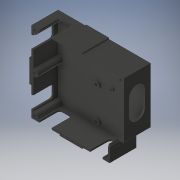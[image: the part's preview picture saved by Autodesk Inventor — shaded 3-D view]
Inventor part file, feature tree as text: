
AUTODESK INVENTOR PART (.ipt)
format: ipt  version: 2019.4 (Build 234330000, 330)  size: 476,160 bytes
history: native  units: mm
features: extrude x19, hole x4, sketch x3, fillet x1, projected_geometry x1
ambient origin geometry x8: Origin, YZ Plane, XZ Plane, XY Plane, X Axis, Y Axis, Z Axis, Center Point
bodies: Solid1 (feature_tree)
feature tree (28):
  sketch  "Sketch1"  dims[d0=147.0mm d1=128.0mm]
  extrude  "Extrusion1"  Depth=128.0mm
  extrude  "Extrusion2"  Depth=37.0mm
  extrude  "Extrusion3"  Depth=2.0mm
  extrude  "Extrusion4"  Depth=5.0mm
  extrude  "Extrusion5"  Depth=5.0mm
  extrude  "Extrusion6"  Depth=2.0mm
  extrude  "Extrusion7"  Depth=5.0mm
  extrude  "Extrusion8"  Depth=5.0mm
  extrude  "Extrusion9"  Depth=22.5mm
  extrude  "Extrusion10"  Depth=5.0mm
  extrude  "Extrusion11"  Depth=22.5mm
  extrude  "Extrusion12"  Depth=22.5mm
  sketch  "Sketch2"  dims[d7=37.0mm d8=18.5mm]
  extrude  "Extrusion13"  Depth=5.0mm
  extrude  "Extrusion14"  Depth=5.0mm
  extrude  "Extrusion15"  Depth=25.0mm
  fillet  "Fillet1"  Radius=25.0mm
  hole  "Hole1"  [1 undecoded]
  extrude  "Extrusion16"  Depth=5.0mm
  extrude  "Extrusion17"  Depth=5.0mm
  hole  "Hole2"  [1 undecoded]
  extrude  "Extrusion18"  Depth=5.0mm
  hole  "Hole3"  [1 undecoded]
  extrude  "Extrusion19"  Depth=2.5mm
  hole  "Hole4"  [1 undecoded]
  projected_geometry  "Projected Loop1"
  sketch  "Sketch3"  dims[d9=3.0mm d10=2.0mm d11=36.0mm d12=45.0mm d13=2.0mm d14=36.0mm d15=45.0mm d16=22.5mm d17=39.4mm d18=22.5mm d19=22.5mm d20=142.0mm d21=123.0mm d22=25.0mm d23=25.0mm d24=25.0mm d25=5.0mm d26=5.0mm d27=5.0mm d28=5.0mm d29=2.5mm d30=2.5mm d31=1.25mm d32=2.5mm d33=0.0mm d34=45.0mm d35=0.0mm d36=45.0mm d37=0.0mm d38=45.0mm d39=0.0mm d40=45.0mm d41=0.0mm d42=45.0mm d43=0.0mm d44=45.0mm d45=0.0mm d46=2.5mm d47=0.0mm d48=45.0mm d49=0.0mm d50=45.0mm d51=0.0mm d52=45.0mm d53=0.0mm d54=45.0mm d55=0.0mm d56=2.5mm d57=0.0mm d58=45.0mm d59=45.0mm d60=45.0mm d61=45.0mm d62=20.0mm d63=20.0mm d64=20.0mm d65=20.0mm d66=12.5mm d67=12.5mm d68=12.5mm d69=20.0mm d70=12.5mm d71=35.0mm d72=0.0mm d73=25.0mm d74=25.0mm d75=20.0mm d76=35.355339mm d77=35.0mm d78=0.0mm d79=5.0mm d80=4.0mm d81=6.0mm d82=4.0mm d83=2.0mm d84=90.0deg d85=8.0mm d86=0.0mm d87=12.5mm d88=90.0deg d89=25.0mm d90=35.0mm d91=0.0mm d92=5.0mm d93=5.0mm d94=42.5mm d95=0.0mm d96=5.0mm d97=5.0mm d98=4.0mm d99=6.0mm d100=4.0mm d101=2.0mm d102=90.0deg d103=8.0mm d104=0.0mm d105=27.94mm d106=52.07mm d107=48.243mm d108=50.8mm d109=1.27mm d110=5.08mm d111=3.0mm d112=12.5mm d113=6.5mm d114=6.5mm d115=6.5mm d116=6.5mm d117=5.0mm d118=0.0mm d119=3.0mm d120=6.0mm d121=5.5mm d122=3.0mm d123=90.0deg d124=5.0mm d125=0.0mm d126=63.0mm d127=50.0mm d128=50.0mm d129=43.0mm d130=12.0mm d131=12.0mm d132=37.5mm d133=5.0mm d134=0.0mm d135=4.0mm d136=6.0mm d137=8.5mm d138=4.0mm d139=90.0deg d140=5.0mm d141=0.0mm]
note: 4 required parameter values undecoded (feature->parameter linkage not recoverable at this tier; creation-order binding heuristic only, values carry confidence <= 0.55)
